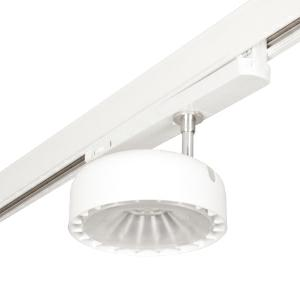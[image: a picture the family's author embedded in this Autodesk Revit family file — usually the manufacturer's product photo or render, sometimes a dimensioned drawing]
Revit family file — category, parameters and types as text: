
# Revit family: 3f_filippi_-_3f_emilio_track_ellittico_-_meat_bread_crisp_3f_filippi_-_47628_-_3f_emilio_tk_led_2000-bread_ell_479a
name_source: partatom
category: Lighting Fixtures
units: mm (PartAtom-declared; Revit-internal decimal feet)

## family parameters
Cut with Voids When Loaded = No
Host = Face
Light Source = No
Part Type = Normal
Room Calculation Point = No
Round Connector Dimension = Use Diameter
Shared = No

## types (1)
- 3F Filippi - 3F Emilio Track Ellittico - Meat/Bread/Crisp (1 x LED, 1998 lm, 35 W, 2400 K)
    Apparent Load = 35 VA
    Approval mark = CE
    CIE Flux Codes = 82 95 99 100 100
    Color Rendering = 90
    Color Temperature = 2400 K
    Control Gear = Electronic ballast
    Default Elevation = 1800 mm
    Description = Adjustable spot light with minimal dimensions for accent lighting, to be integrated into the busbar.

ILLUMINOTECHNICAL
Luminous efficiency 100% (DLOR 100%, ULOR 0%).
Initial luminous flux of the luminaire 1998 lm.
Symmetrical and elliptical distribution.
Tabular UGR (CIE 117 - 4H-8H; S=0.25H; 70/50/20): RUG 21 - 24.3.
Beam angle: 54° - 89°.
Luminous efficacy 57 lm/W.
Lifetime (L85/B20): 30000 h. (tq+25°C)
Lifetime (L75/B20): 50000 h. (tq+25°C)
Sudden decreased luminous flux after 50000 hours: 0% (C0).
Photobiological safety in compliance with IEC/TR 62778: RG1 low risk, (IEC 62471).
In compliance with IEC/EN 62722-2-1 - IEC/EN 62717 standards.

SOURCE
2000/BREAD compact LED module, specifically designed for bakeries.
Energy efficiency class (UE 2019/2020 - UE 2019/2015): E.
CIE 13.3 Colour rendering index: CRI >90 (R9 >50%).
IES TM-30 Fidelity Index: Rf = 92 Rg = 103.
CCT nominal colour temperature 2400 K.
Colour initial tolerance (MacAdam): SDCM 3.
Zhaga Book 3 compliant.

MECHANICAL
Wired unit in white polycarbonate with busbar adaptor.
Single-piece in die-cast aluminium with passive dissipation, white colour, with perimeter cooling slots on upper edge, giving a crown of light effect to the fitting.
Invisible lock for positioning the luminous flux.
Lens made from transparent methacrylate (PMMA) with glossy surface and differentiated photo-etched.
Positioning arm in galvanised brass with sphere to allow for vertical positioning at angles from 0° to 90° and horizontal positioning from 0° to 290°.
Dimensions: diameter 130 mm, length 230 mm, height 105 mm. Weight 0.825 kg.
IP20 protection degree.
Glow-wire test resistance 650°C.

ELECTRICAL
Wiring unit separate from the body, invisible and integrated into the busbar.
Halogen Free electronic wiring 230V-50/60Hz, power factor 0.95, THD <25%, constant output current, SELV, class II, 1 driver.
Power of the luminaire 35 W.
ENEC - CE.
SAFE FLICKER: PstLM=<1 and SVM=<0.4 (IEC TR 61547-1 and IEC TR 63158), to ensure a more comfortable and safe light.
Ambient temperature from 0°C to +25°C.
Temperature class T6 max 85°C.
Relative humidity UR: <85%.

INSTALLATION
Track.

APPLICATIONS
Transit areas, spotlighting in commercial environments, exhibition areas, restaurants, shops and shop windows.

WARNING
Luminaire designed for disposal/recycling at end-of-life.
Replaceable (LED only) light source by a professional. Replaceable control gear by a professional.
    Height = 105 mm
    Lamp = 1 x LED
    Lamp Light Flux = 1998 lm
    Lamp Power = 35 W
    Lamp count = 1
    Length = 230 mm
    Lifetime = 50000 h
    Luminous efficacy = 57 lm/W
    Manufacturer = 3F Filippi
    ModVariant = No
    Model = 3F Filippi - 47628 - 3F Emilio TK LED 2000-BREAD ELL
    Mounting Place = Ceiling
    Mounting Type = Rail mounted
    Number of Poles = 1
    OnlyDefault = Yes
    Power Factor = 1
    Product Name = 3F Filippi - 3F Emilio Track Ellittico - Meat/Bread/Crisp
    Product group = track mounted spotlight
    ProductGroupID = 12
    Protection Class = Protection class II
    Protection Degree = IP 20
    RLX_Detail_Level = 1
    RLX_Emergency_Light_Flux = 0 lm
    RLX_Emergency_Type = 0
    RLX_Emergency_Type_DB = No
    RlxData = <blob elided: 152257 chars, md5=0f907f22>
    Socket = socket
    Standby Power = 0 W
    System Light Flux = 1998 lm
    System Power = 35 W
    Type Comments = Product without accessories
    Type Image = 3ffilippi_47628.jpg
    URL = http://relux.com
    VarID = ---
    Voltage = 0 V
    Weight = 0.00 kg
    Width = 130 mm

## geometry (parser evidence)
native form markers: Blend x4, Sweep x14
no freeform markers — native parametric forms only
